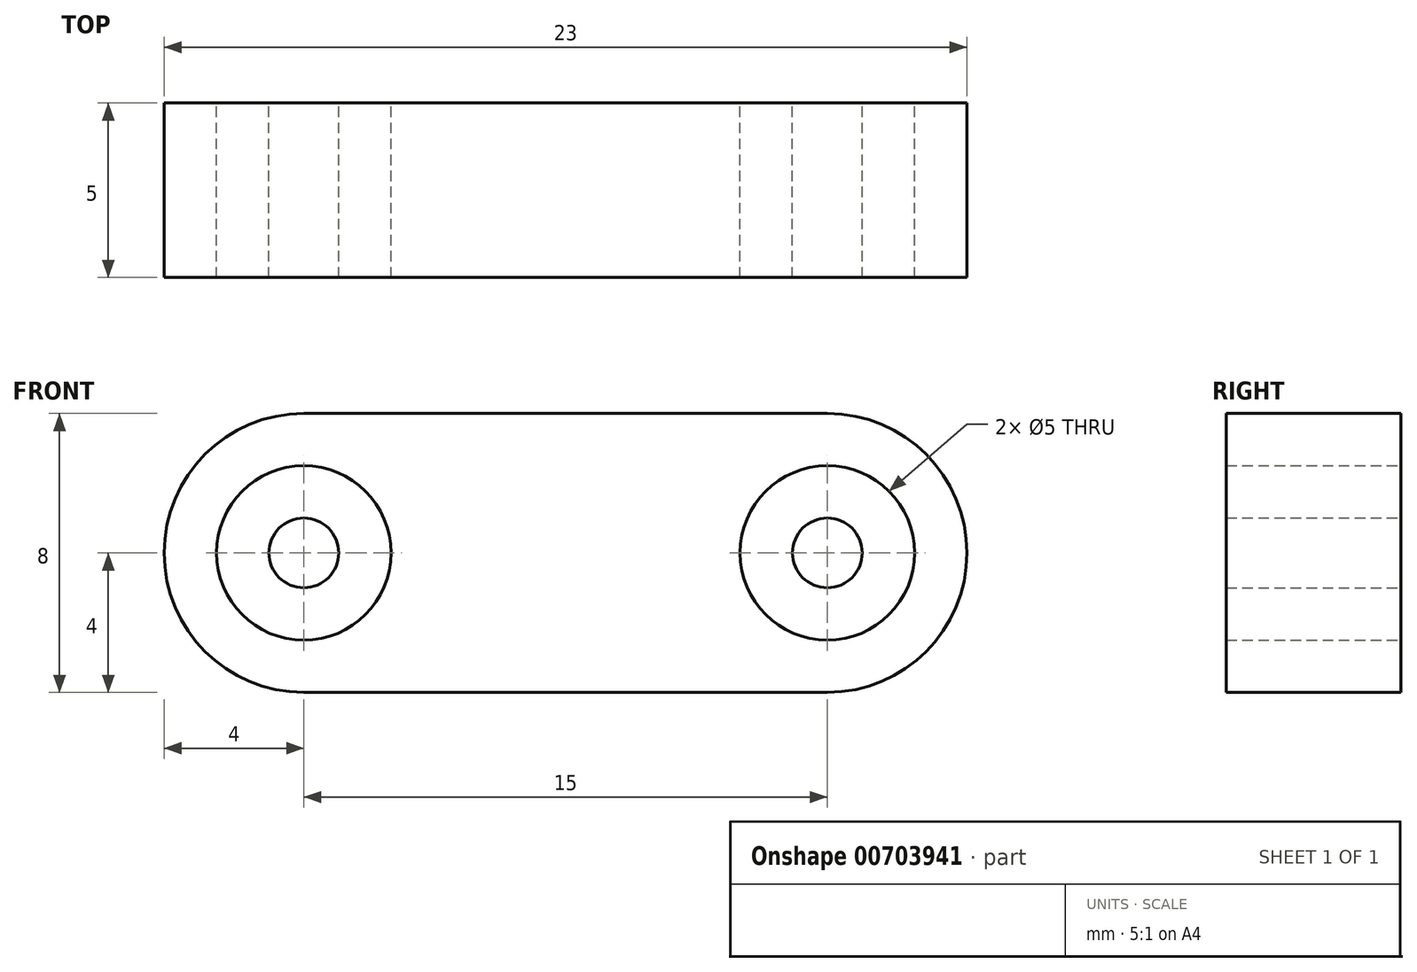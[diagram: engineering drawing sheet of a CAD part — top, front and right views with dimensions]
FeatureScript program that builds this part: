
annotation { "Feature Type Name" : "Feature", "Feature Type Description" : "" }
export const myFeature = defineFeature(function(context is Context, id is Id, definition is map)
    precondition{}
    {
        {
            var Q0;
            Q0=qCreatedBy(makeId("Front.planeOp"),FACE);
            var sketch = newSketch(context, id + "F0", { "sketchPlane" : qUnion([Q0])});
            skArc(sketch, "E0", {"start": v(0, 4) * mm, "mid": v(-4, 0) * mm, "end": v(0, -4) * mm});
            skCircle(sketch, "E1", {"center": v(0, 0) * mm, "radius": 2.5 * mm});
            skCircle(sketch, "E2", {"center": v(0, 0) * mm, "radius": 1 * mm});
            skArc(sketch, "E3", {"start": v(15, -4) * mm, "mid": v(19, 0) * mm, "end": v(15, 4) * mm});
            skCircle(sketch, "E4", {"center": v(15, 0) * mm, "radius": 2.5 * mm});
            skCircle(sketch, "E5", {"center": v(15, 0) * mm, "radius": 1 * mm});
            skLineSegment(sketch, "E6", {"start": v(0, 4) * mm, "end": v(15, 4) * mm});
            skLineSegment(sketch, "E7", {"start": v(0, -4) * mm, "end": v(15, -4) * mm});
            skSolve(sketch);
        }
        {
            var Q0;
            Q0 = qSketchRegion(id + "F0", true);
            var Q1;
            Q1=makeQuery(id+"F0.imprint","IMPRINT",FACE,{"disambiguationData":[TD([[makeQuery(id+"F0.imprint","IMPRINT",EDGE,{"derivedFrom":sQuery(id+"F0.wireOp",EDGE,"E2")}),1.0]])]});
            var Q2;
            Q2=makeQuery(id+"F0.imprint","IMPRINT",FACE,{"disambiguationData":[TD([[makeQuery(id+"F0.imprint","IMPRINT",EDGE,{"derivedFrom":sQuery(id+"F0.wireOp",EDGE,"E5")}),1.0]])]});
            extrude(context, id + "F1", {"entities" : qUnion([Q0, Q1, Q2]), "depth" : 5 * mm, "offsetDistance" : 25 * mm});
        }
    });
